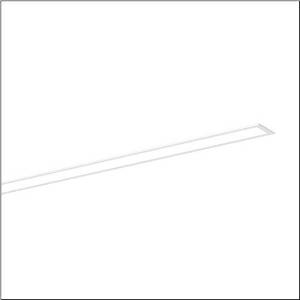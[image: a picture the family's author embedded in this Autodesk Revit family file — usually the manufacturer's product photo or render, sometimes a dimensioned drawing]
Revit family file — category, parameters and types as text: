
# Revit family: silica_21_51mx10db32wb
name_source: partatom
category: Lighting Fixtures
units: mm (PartAtom-declared; Revit-internal decimal feet)

## family parameters
Cut with Voids When Loaded = No
Host = Face
Light Source = No
Part Type = Normal
Room Calculation Point = No
Round Connector Dimension = Use Diameter
Shared = No

## types (1)
- --- (1 x LED, 3000 lm, 20.2 W, 3000K)
    Apparent Load = 20 VA
    CIE Flux Codes = 48 79 96 100 100
    Color Rendering = 80
    Color Temperature = 3000K
    Default Elevation = 1800 mm
    Description = Silica 21, office luminaire, primary optical cover: cover, of PMMA, opal, light emission: direct distribution, primary light characteristic: symmetric, installation type: recessed, LED, rated luminous flux: 3.000lm, luminous efficacy: 149lm/W, light colour: 830, colour temperature: 3000K, control gear: DALI 2, with terminal, 3+2-pole, max. 2.5mm², mains connection: 220..240V, AC, 50/60Hz, luminaire housing, of aluminium, traffic white (RAL 9016), length: 1.528mm, width: 79mm, height: 53mm, protection rating (complete): IP20, insulation class (complete): insulation class I (protective earthing), certification: CE, ENEC, VDE, permissible operating ambient temperature: 0..+35°C, standard: EN 50419, packaging unit: 1 piece
    Height = 0 mm  [stored 0 ft]
    Lamp = 1 x LED
    Lamp Light Flux = 3000 lm
    Lamp Power = 20.2 W
    Lamp count = 1
    Length = 1527 mm
    Luminous efficacy = 149 lm/W
    Manufacturer = Siteco
    ModVariant = No
    Model = 51MX10DB32WB
    Mounting Place = Ceiling
    Mounting Type = Recessed
    Number of Poles = 1
    OnlyDefault = Yes
    Power Factor = 1
    Product Name = Silica 21
    Product group = office luminaire | ceiling recessed
    ProductGroupID = 400
    Protection Class = Protection class I
    Protection Degree = IP 20
    RLX_Detail_Level = 1
    RLX_Emergency_Light_Flux = 0 lm
    RLX_Emergency_Type = 0
    RLX_Emergency_Type_DB = No
    RlxData = <blob elided: 20857 chars, md5=4bdf12aa>
    Socket = socket
    Standby Power = 0 W
    System Light Flux = 3000 lm
    System Power = 20 W
    Type Comments = factory setting: luminous flux: 100 % | dim-lin: 254 | 233 mA
    Type Image = l_1335891.jpg
    URL = http://relux.com
    VarID = @adj_117805
    Voltage = 0 V
    Weight = 0.00 kg
    Width = 79 mm

note: [stored X ft] marks values corroborated as IEEE doubles in the binary element streams (Revit-internal decimal feet)

## geometry (parser evidence)
native form markers: Blend x4, Sweep x11
no freeform markers — native parametric forms only
